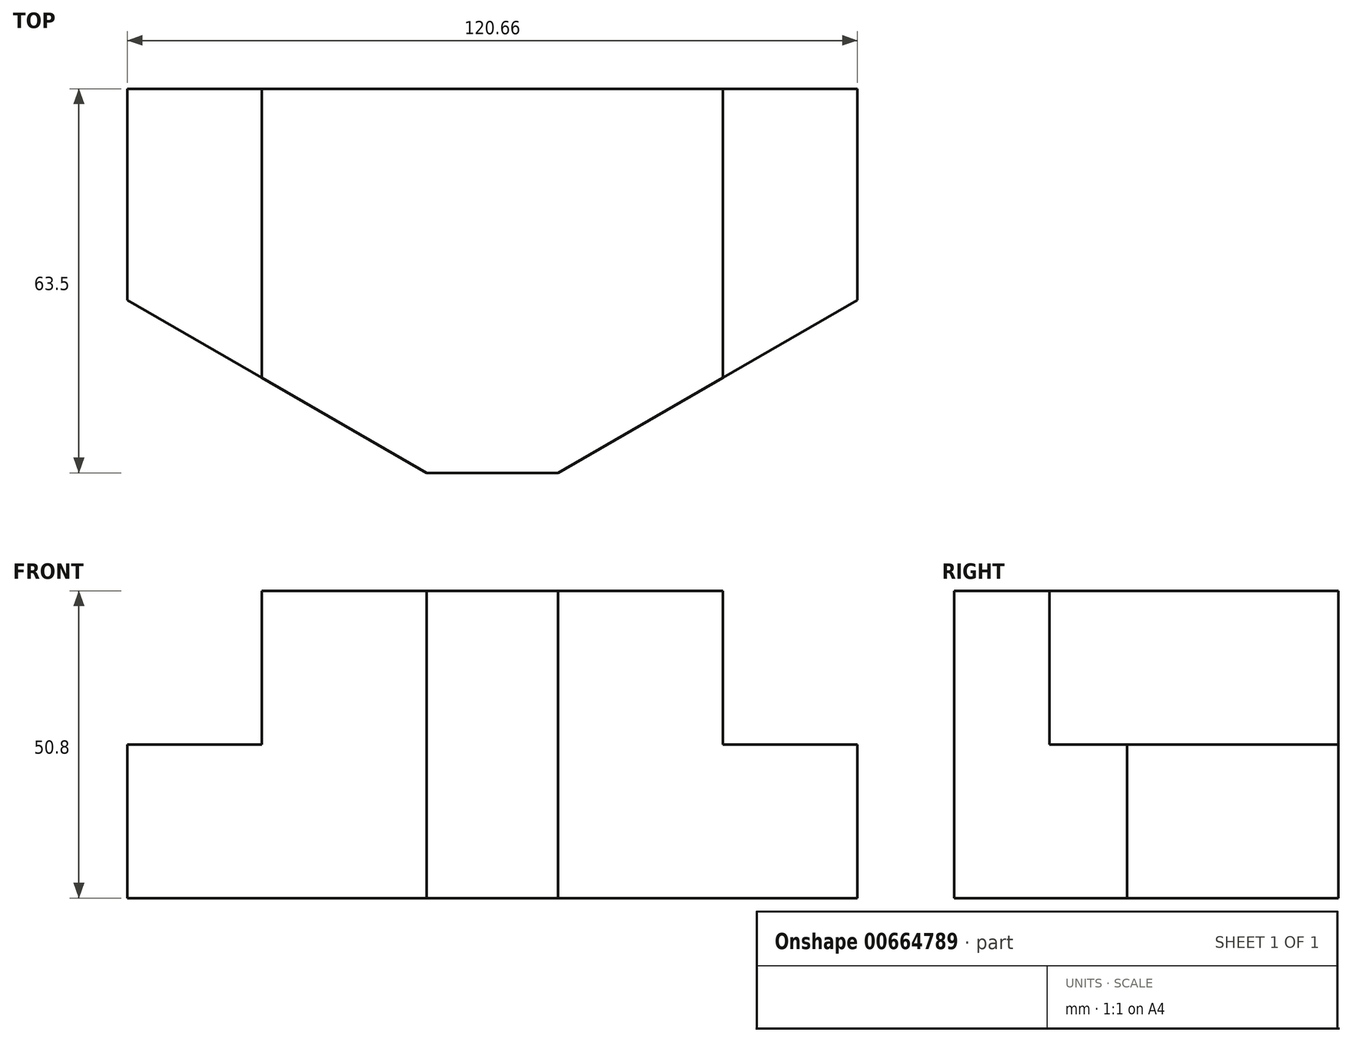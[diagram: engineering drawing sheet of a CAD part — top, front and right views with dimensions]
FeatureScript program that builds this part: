
annotation { "Feature Type Name" : "Feature", "Feature Type Description" : "" }
export const myFeature = defineFeature(function(context is Context, id is Id, definition is map)
    precondition{}
    {
        {
            var Q0;
            Q0=qCreatedBy(makeId("Top.planeOp"),FACE);
            var sketch = newSketch(context, id + "F0", { "sketchPlane" : qUnion([Q0])});
            skLineSegment(sketch, "E0.bottom", {"start": v(-60.33, 31.75) * mm, "end": v(60.33, 31.75) * mm});
            skLineSegment(sketch, "E0.top", {"start": v(-60.33, -31.75) * mm, "end": v(60.33, -31.75) * mm});
            skLineSegment(sketch, "E0.left", {"start": v(-60.33, 31.75) * mm, "end": v(-60.33, -31.75) * mm});
            skLineSegment(sketch, "E0.right", {"start": v(60.33, 31.75) * mm, "end": v(60.33, -31.75) * mm});
            skPoint(sketch, "E0.middle", {"position": v(0, 0) * mm});
            skPoint(sketch, "E1", {"position": v(60.33, -3.18) * mm});
            skPoint(sketch, "E2", {"position": v(-60.33, -3.18) * mm});
            skLineSegment(sketch, "E3", {"start": v(-60.33, -3.18) * mm, "end": v(-10.83, -31.75) * mm});
            skLineSegment(sketch, "E4", {"start": v(60.33, -3.18) * mm, "end": v(10.83, -31.75) * mm});
            skSolve(sketch);
        }
        {
            var Q0;
            {var subQ1=sQuery(id+"F0.wireOp",EDGE,"E0.bottom");Q0=makeQuery(id+"F0.imprint","IMPRINT",FACE,{"disambiguationData":[TD([[makeQuery(id+"F0.imprint","IMPRINT",EDGE,{"derivedFrom":subQ1}),-1.0]])]});}
            extrude(context, id + "F1", {"entities" : qUnion([Q0]), "depth" : 50.8 * mm, "offsetDistance" : 25.4 * mm});
        }
        {
            var Q0;
            Q0=qCreatedBy(makeId("Front.planeOp"),FACE);
            var sketch = newSketch(context, id + "F2", { "sketchPlane" : qUnion([Q0])});
            skLineSegment(sketch, "E5.bottom", {"start": v(-38.1, 25.4) * mm, "end": v(-60.33, 25.4) * mm});
            skLineSegment(sketch, "E5.top", {"start": v(-38.1, 50.8) * mm, "end": v(-60.33, 50.8) * mm});
            skLineSegment(sketch, "E5.left", {"start": v(-38.1, 25.4) * mm, "end": v(-38.1, 50.8) * mm});
            skLineSegment(sketch, "E5.right", {"start": v(-60.33, 25.4) * mm, "end": v(-60.33, 50.8) * mm});
            skSolve(sketch);
        }
        {
            var Q0;
            Q0 = qSketchRegion(id + "F2", true);
            extrude(context, id + "F3", {"entities" : qUnion([Q0]), "operationType" : NewBodyOperationType.REMOVE, "endBound" : BoundingType.SYMMETRIC, "oppositeDirection" : true, "depth" : 89.4 * mm, "offsetDistance" : 25.4 * mm});
        }
        {
            var Q0;
            Q0=qCreatedBy(makeId("Front.planeOp"),FACE);
            var sketch = newSketch(context, id + "F4", { "sketchPlane" : qUnion([Q0])});
            skLineSegment(sketch, "E6.bottom", {"start": v(60.33, 50.8) * mm, "end": v(38.1, 50.8) * mm});
            skLineSegment(sketch, "E6.top", {"start": v(60.33, 25.4) * mm, "end": v(38.1, 25.4) * mm});
            skLineSegment(sketch, "E6.left", {"start": v(60.33, 50.8) * mm, "end": v(60.33, 25.4) * mm});
            skLineSegment(sketch, "E6.right", {"start": v(38.1, 50.8) * mm, "end": v(38.1, 25.4) * mm});
            skSolve(sketch);
        }
        {
            var Q0;
            Q0 = qSketchRegion(id + "F4", true);
            extrude(context, id + "F5", {"entities" : qUnion([Q0]), "operationType" : NewBodyOperationType.REMOVE, "endBound" : BoundingType.SYMMETRIC, "oppositeDirection" : true, "depth" : 75.18 * mm, "offsetDistance" : 25.4 * mm});
        }
    });
